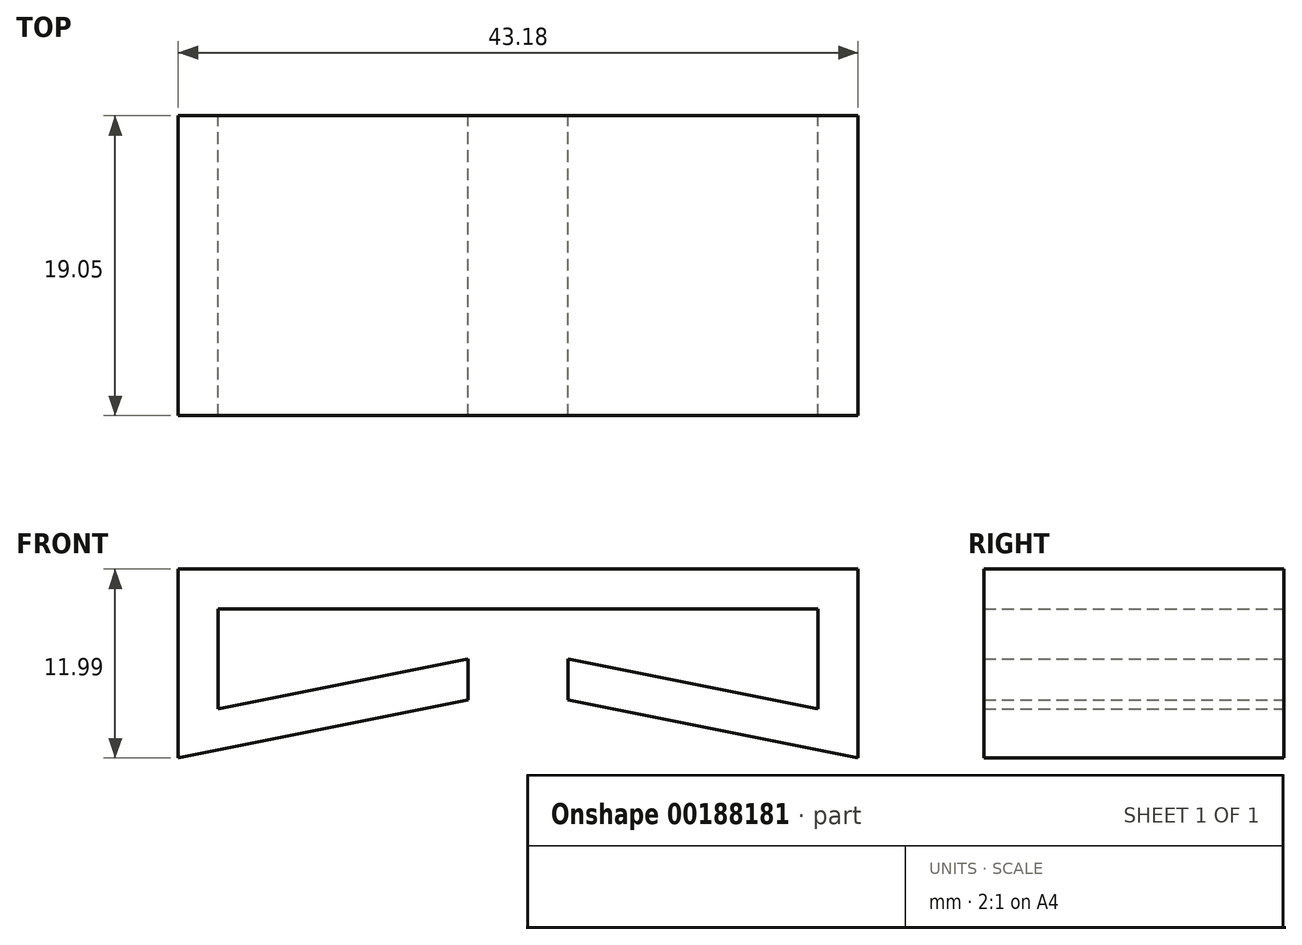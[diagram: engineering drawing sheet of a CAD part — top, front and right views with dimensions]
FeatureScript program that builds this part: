
annotation { "Feature Type Name" : "Feature", "Feature Type Description" : "" }
export const myFeature = defineFeature(function(context is Context, id is Id, definition is map)
    precondition{}
    {
        {
            var Q0;
            Q0=qCreatedBy(makeId("Front.planeOp"),FACE);
            var sketch = newSketch(context, id + "F0", { "sketchPlane" : qUnion([Q0])});
            skLineSegment(sketch, "E0", {"start": v(3.18, -5.72) * mm, "end": v(19.05, -8.9) * mm});
            skLineSegment(sketch, "E1", {"start": v(19.05, -8.9) * mm, "end": v(19.05, -2.54) * mm});
            skLineSegment(sketch, "E2", {"start": v(19.05, -2.54) * mm, "end": v(-19.05, -2.54) * mm});
            skLineSegment(sketch, "E3", {"start": v(-19.05, -2.54) * mm, "end": v(-19.05, -8.9) * mm});
            skLineSegment(sketch, "E4", {"start": v(-19.05, -8.9) * mm, "end": v(-3.17, -5.72) * mm});
            skLineSegment(sketch, "E5.0", {"start": v(-21.59, -11.99) * mm, "end": v(-3.17, -8.3) * mm});
            skLineSegment(sketch, "E5.1", {"start": v(3.18, -8.3) * mm, "end": v(21.6, -11.99) * mm});
            skLineSegment(sketch, "E5.2", {"start": v(21.59, -11.99) * mm, "end": v(21.59, 0) * mm});
            skLineSegment(sketch, "E5.3", {"start": v(21.59, 0) * mm, "end": v(-21.59, 0) * mm});
            skLineSegment(sketch, "E5.4", {"start": v(-21.59, 0) * mm, "end": v(-21.59, -11.99) * mm});
            skLineSegment(sketch, "E6", {"start": v(3.18, -5.72) * mm, "end": v(3.18, -8.3) * mm});
            skLineSegment(sketch, "E7", {"start": v(-3.17, -5.72) * mm, "end": v(-3.17, -8.3) * mm});
            skSolve(sketch);
        }
        {
            var Q0;
            Q0=makeQuery(id+"F0.imprint","IMPRINT",FACE,{"disambiguationData":[TD([[makeQuery(id+"F0.imprint","IMPRINT",EDGE,{"derivedFrom":sQuery(id+"F0.wireOp",EDGE,"E0")}),-1.0]])]});
            extrude(context, id + "F1", {"entities" : qUnion([Q0]), "depth" : 19.05 * mm});
        }
    });
